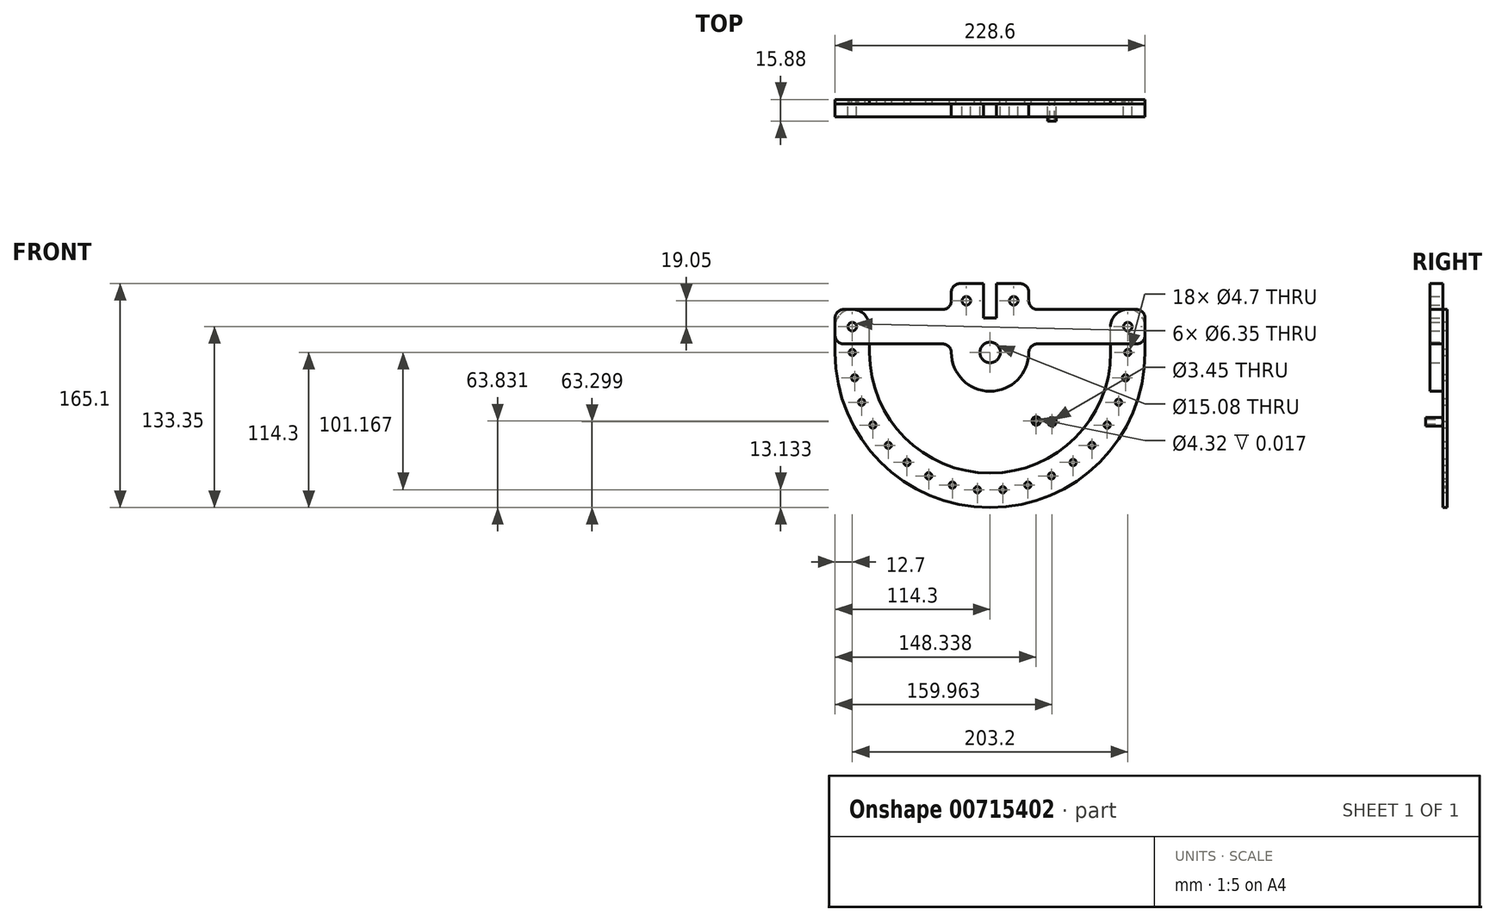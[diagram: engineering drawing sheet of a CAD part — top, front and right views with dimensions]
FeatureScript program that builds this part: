
annotation { "Feature Type Name" : "Feature", "Feature Type Description" : "" }
export const myFeature = defineFeature(function(context is Context, id is Id, definition is map)
    precondition{}
    {
        {
            var Q0;
            Q0=qCreatedBy(makeId("Front.planeOp"),FACE);
            var sketch = newSketch(context, id + "F0", { "sketchPlane" : qUnion([Q0])});
            skArc(sketch, "E0", {"start": v(-114.3, 0) * mm, "mid": v(0, -114.3) * mm, "end": v(114.3, 0) * mm});
            skArc(sketch, "E1", {"start": v(88.9, 0) * mm, "mid": v(0, -88.9) * mm, "end": v(-88.9, 0) * mm});
            skLineSegment(sketch, "E2", {"start": v(-114.3, 0) * mm, "end": v(-114.3, 19.05) * mm});
            skLineSegment(sketch, "E3", {"start": v(-88.9, 0) * mm, "end": v(-88.9, 19.05) * mm});
            skArc(sketch, "E4", {"start": v(-114.3, 19.05) * mm, "mid": v(-101.6, 31.75) * mm, "end": v(-88.9, 19.05) * mm});
            skArc(sketch, "E5.MirrorCS", {"start": v(114.3, 19.05) * mm, "mid": v(101.6, 31.75) * mm, "end": v(88.9, 19.05) * mm});
            skLineSegment(sketch, "E6.MirrorCS", {"start": v(88.9, 0) * mm, "end": v(88.9, 19.05) * mm});
            skLineSegment(sketch, "E7.MirrorCS", {"start": v(114.3, 0) * mm, "end": v(114.3, 19.05) * mm});
            skCircle(sketch, "E8", {"center": v(101.6, 19.05) * mm, "radius": 3.18 * mm});
            skCircle(sketch, "E9", {"center": v(101.6, 0) * mm, "radius": 2.35 * mm});
            skCircle(sketch, "E10.1.0", {"center": v(99.87, -18.67) * mm, "radius": 2.35 * mm});
            skCircle(sketch, "E10.2.0", {"center": v(94.74, -36.7) * mm, "radius": 2.35 * mm});
            skCircle(sketch, "E10.3.0", {"center": v(86.38, -53.49) * mm, "radius": 2.35 * mm});
            skCircle(sketch, "E10.4.0", {"center": v(75.08, -68.45) * mm, "radius": 2.35 * mm});
            skCircle(sketch, "E10.5.0", {"center": v(61.23, -81.08) * mm, "radius": 2.35 * mm});
            skCircle(sketch, "E10.6.0", {"center": v(45.29, -90.95) * mm, "radius": 2.35 * mm});
            skCircle(sketch, "E10.7.0", {"center": v(27.8, -97.72) * mm, "radius": 2.35 * mm});
            skCircle(sketch, "E10.8.0", {"center": v(9.37, -101.17) * mm, "radius": 2.35 * mm});
            skCircle(sketch, "E10.9.0", {"center": v(-9.37, -101.17) * mm, "radius": 2.35 * mm});
            skCircle(sketch, "E10.10.0", {"center": v(-27.8, -97.72) * mm, "radius": 2.35 * mm});
            skCircle(sketch, "E10.11.0", {"center": v(-45.29, -90.95) * mm, "radius": 2.35 * mm});
            skCircle(sketch, "E10.12.0", {"center": v(-61.23, -81.08) * mm, "radius": 2.35 * mm});
            skCircle(sketch, "E10.13.0", {"center": v(-75.08, -68.45) * mm, "radius": 2.35 * mm});
            skCircle(sketch, "E10.14.0", {"center": v(-86.38, -53.49) * mm, "radius": 2.35 * mm});
            skCircle(sketch, "E10.15.0", {"center": v(-94.74, -36.7) * mm, "radius": 2.35 * mm});
            skCircle(sketch, "E10.16.0", {"center": v(-99.87, -18.67) * mm, "radius": 2.35 * mm});
            skCircle(sketch, "E10.17.0", {"center": v(-101.6, 0) * mm, "radius": 2.35 * mm});
            skLineSegment(sketch, "E10.anchor1", {"start": v(0, 0) * mm, "end": v(101.6, 0) * mm, "construction": true});
            skLineSegment(sketch, "E10.anchor2", {"start": v(0, 0) * mm, "end": v(-101.6, 0) * mm, "construction": true});
            skCircle(sketch, "E11", {"center": v(-101.6, 19.05) * mm, "radius": 3.18 * mm});
            skSolve(sketch);
        }
        {
            var Q0;
            Q0=qCreatedBy(makeId("Front.planeOp"),FACE);
            var sketch = newSketch(context, id + "F1", { "sketchPlane" : qUnion([Q0])});
            skCircle(sketch, "E12", {"center": v(0, 0) * mm, "radius": 7.54 * mm});
            skArc(sketch, "E13", {"start": v(28.58, 0) * mm, "mid": v(0, -28.58) * mm, "end": v(-28.58, 0) * mm});
            skLineSegment(sketch, "E14", {"start": v(28.58, 0) * mm, "end": v(28.58, 0) * mm});
            skLineSegment(sketch, "E15", {"start": v(34.92, 6.35) * mm, "end": v(107.95, 6.35) * mm});
            skLineSegment(sketch, "E16", {"start": v(114.3, 12.7) * mm, "end": v(114.3, 25.4) * mm});
            skLineSegment(sketch, "E17", {"start": v(-34.93, 31.75) * mm, "end": v(-107.95, 31.75) * mm});
            skPoint(sketch, "E18.visualSharp", {"position": v(28.58, 6.35) * mm});
            skArc(sketch, "E18.filletArc", {"start": v(34.92, 6.35) * mm, "mid": v(30.43, 4.5) * mm, "end": v(28.57, 0) * mm});
            skPoint(sketch, "E19.visualSharp", {"position": v(114.3, 6.35) * mm});
            skArc(sketch, "E19.filletArc", {"start": v(107.95, 6.35) * mm, "mid": v(112.44, 8.2) * mm, "end": v(114.3, 12.7) * mm});
            skPoint(sketch, "E20.visualSharp", {"position": v(114.3, 31.75) * mm});
            skArc(sketch, "E20.filletArc", {"start": v(114.3, 25.4) * mm, "mid": v(112.44, 29.9) * mm, "end": v(107.95, 31.75) * mm});
            skLineSegment(sketch, "E21.MirrorCS", {"start": v(-28.58, 0) * mm, "end": v(-28.58, 0) * mm});
            skPoint(sketch, "E22.MirrorP", {"position": v(-28.58, 6.35) * mm});
            skArc(sketch, "E23.MirrorCS", {"start": v(-34.92, 6.35) * mm, "mid": v(-30.43, 4.5) * mm, "end": v(-28.57, 0) * mm});
            skLineSegment(sketch, "E24.MirrorCS", {"start": v(-34.92, 6.35) * mm, "end": v(-107.95, 6.35) * mm});
            skArc(sketch, "E25.MirrorCS", {"start": v(-107.95, 6.35) * mm, "mid": v(-112.44, 8.2) * mm, "end": v(-114.3, 12.7) * mm});
            skLineSegment(sketch, "E26.MirrorCS", {"start": v(-114.3, 12.7) * mm, "end": v(-114.3, 25.4) * mm});
            skArc(sketch, "E27.MirrorCS", {"start": v(-114.3, 25.4) * mm, "mid": v(-112.44, 29.9) * mm, "end": v(-107.95, 31.75) * mm});
            skCircle(sketch, "E28.0", {"center": v(-101.6, 19.05) * mm, "radius": 3.18 * mm});
            skCircle(sketch, "E28.1", {"center": v(101.6, 19.05) * mm, "radius": 3.18 * mm});
            skCircle(sketch, "E29", {"center": v(-17.46, 38.1) * mm, "radius": 3.18 * mm});
            skLineSegment(sketch, "E30", {"start": v(-28.58, 38.1) * mm, "end": v(-28.58, 44.45) * mm});
            skLineSegment(sketch, "E31", {"start": v(-22.23, 50.8) * mm, "end": v(22.22, 50.8) * mm});
            skLineSegment(sketch, "E32", {"start": v(28.58, 44.45) * mm, "end": v(28.58, 38.1) * mm});
            skArc(sketch, "E33.filletArc", {"start": v(-34.93, 31.75) * mm, "mid": v(-30.43, 33.6) * mm, "end": v(-28.57, 38.1) * mm});
            skPoint(sketch, "E34.visualSharp", {"position": v(-28.58, 50.8) * mm});
            skArc(sketch, "E34.filletArc", {"start": v(-22.23, 50.8) * mm, "mid": v(-26.72, 48.94) * mm, "end": v(-28.58, 44.45) * mm});
            skPoint(sketch, "E35.visualSharp", {"position": v(28.58, 50.8) * mm});
            skArc(sketch, "E35.filletArc", {"start": v(28.58, 44.45) * mm, "mid": v(26.72, 48.94) * mm, "end": v(22.23, 50.8) * mm});
            skLineSegment(sketch, "E36", {"start": v(34.93, 31.75) * mm, "end": v(107.95, 31.75) * mm});
            skPoint(sketch, "E37.visualSharp", {"position": v(28.58, 31.75) * mm});
            skArc(sketch, "E37.filletArc", {"start": v(28.57, 38.1) * mm, "mid": v(30.43, 33.6) * mm, "end": v(34.93, 31.75) * mm});
            skCircle(sketch, "E38.MirrorC", {"center": v(17.46, 38.1) * mm, "radius": 3.18 * mm});
            skLineSegment(sketch, "E39", {"start": v(-4.76, 50.8) * mm, "end": v(-4.76, 25.4) * mm});
            skLineSegment(sketch, "E40.MirrorCS", {"start": v(4.76, 50.8) * mm, "end": v(4.76, 25.4) * mm});
            skLineSegment(sketch, "E41", {"start": v(4.76, 25.4) * mm, "end": v(-4.76, 25.4) * mm});
            skSolve(sketch);
        }
        {
            var Q0;
            Q0=makeQuery(id+"F1.imprint","IMPRINT",FACE,{"disambiguationData":[TD([[makeQuery(id+"F1.imprint","IMPRINT",EDGE,{"derivedFrom":sQuery(id+"F1.wireOp",EDGE,"E12")}),-1.0]])]});
            extrude(context, id + "F2", {"entities" : qUnion([Q0]), "depth" : 9.52 * mm, "offsetDistance" : 25.4 * mm});
        }
        {
            var Q0;
            Q0=makeQuery(id+"F0.imprint","IMPRINT",FACE,{"disambiguationData":[TD([[makeQuery(id+"F0.imprint","IMPRINT",EDGE,{"derivedFrom":sQuery(id+"F0.wireOp",EDGE,"E0")}),1.0]])]});
            extrude(context, id + "F3", {"entities" : qUnion([Q0]), "oppositeDirection" : true, "depth" : 3.17 * mm, "offsetDistance" : 25.4 * mm});
        }
        {
            var Q0;
            Q0=qCreatedBy(makeId("Front.planeOp"),FACE);
            var sketch = newSketch(context, id + "F4", { "sketchPlane" : qUnion([Q0])});
            skCircle(sketch, "E42", {"center": v(45.66, -51) * mm, "radius": 3.18 * mm});
            skCircle(sketch, "E43", {"center": v(34.04, -50.47) * mm, "radius": 3.18 * mm});
            skSolve(sketch);
        }
        {
            var Q0;
            Q0=makeQuery(id+"F4.imprint","IMPRINT",FACE,{"disambiguationData":[TD([[makeQuery(id+"F4.imprint","IMPRINT",EDGE,{"derivedFrom":sQuery(id+"F4.wireOp",EDGE,"E42")}),1.0]])]});
            extrude(context, id + "F5", {"entities" : qUnion([Q0]), "depth" : 12.7 * mm, "offsetDistance" : 25.4 * mm});
        }
        {
            var Q0;
            Q0=makeQuery(id+"F4.imprint","IMPRINT",FACE,{"disambiguationData":[TD([[makeQuery(id+"F4.imprint","IMPRINT",EDGE,{"derivedFrom":sQuery(id+"F4.wireOp",EDGE,"E43")}),1.0]])]});
            extrude(context, id + "F6", {"entities" : qUnion([Q0]), "depth" : 7 / 406.4 * mm, "offsetDistance" : 25.4 * mm});
        }
        {
            var Q0;
            Q0=sQuery(id+"F4.wireOp",VERTEX,"E42.center");
            var Q1;
            Q1=makeQuery(id+"F5.opExtrude","SWEPT_BODY",BODY,{"disambiguationData":[OSD([sQuery(id+"F4.wireOp",EDGE,"E42")])]});
            hole(context, id + "F7", {"style" : HoleStyle.SIMPLE, "endStyle" : HoleEndStyle.THROUGH, "oppositeDirection" : true, "standardTappedOrClearance" : lookupTablePath({ "standard" : "ANSI", "engagement" : "75%", "pitch" : "32 tpi", "size" : "#8", "type" : "Tapped" }), "standardBlindInLast" : lookupTablePath({ "standard" : "ANSI", "engagement" : "75%", "pitch" : "32 tpi", "size" : "#8", "type" : "Tapped" }), "holeDiameter" : 3.45 * mm, "majorDiameter" : 4.17 * mm, "showTappedDepth" : true, "isTappedThrough" : true, "tappedDepth" : 12.7 * mm, "tapClearance" : 3, "locations" : qUnion([Q0]), "scope" : qUnion([Q1])});
        }
        {
            var Q0;
            Q0=sQuery(id+"F4.wireOp",VERTEX,"E43.center");
            var Q1;
            Q1=makeQuery(id+"F6.opExtrude","SWEPT_BODY",BODY,{"disambiguationData":[OSD([sQuery(id+"F4.wireOp",EDGE,"E43")])]});
            hole(context, id + "F8", {"style" : HoleStyle.SIMPLE, "endStyle" : HoleEndStyle.THROUGH, "oppositeDirection" : true, "standardTappedOrClearance" : lookupTablePath({ "standard" : "ANSI", "fit" : "Close", "size" : "#8", "type" : "Clearance" }), "standardBlindInLast" : lookupTablePath({ "fit" : "Close", "standard" : "ANSI", "size" : "#8", "type" : "Clearance" }), "holeDiameter" : 4.32 * mm, "majorDiameter" : 4.17 * mm, "isTappedThrough" : true, "tappedDepth" : 12.7 * mm, "tapClearance" : 3, "locations" : qUnion([Q0]), "scope" : qUnion([Q1])});
        }
    });
